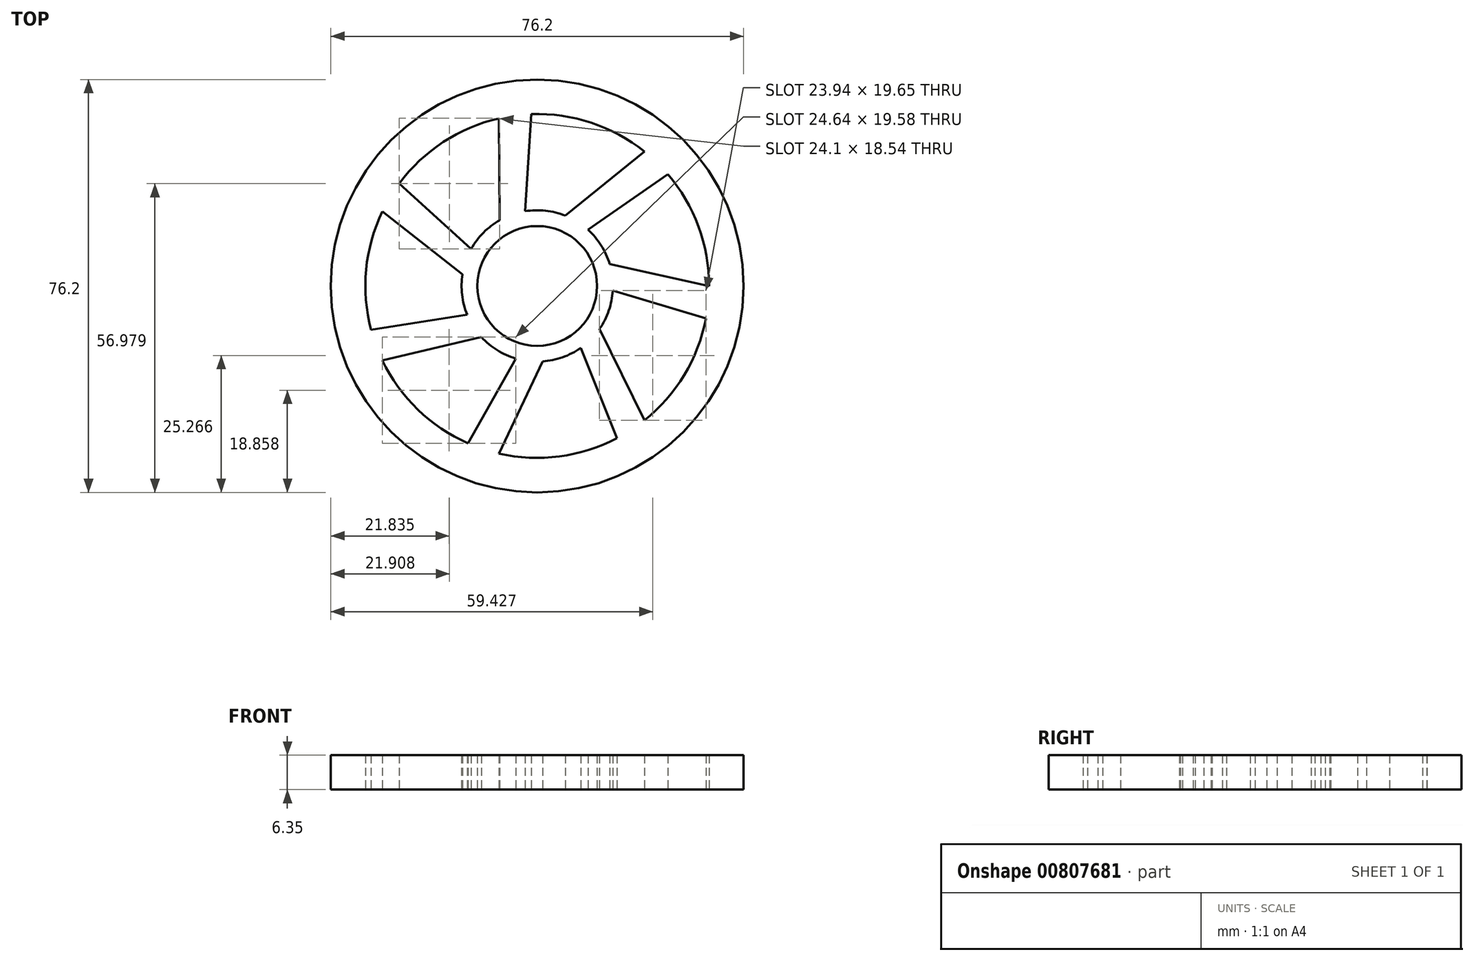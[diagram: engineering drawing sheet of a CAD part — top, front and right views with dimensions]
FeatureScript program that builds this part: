
annotation { "Feature Type Name" : "Feature", "Feature Type Description" : "" }
export const myFeature = defineFeature(function(context is Context, id is Id, definition is map)
    precondition{}
    {
        {
            var Q0;
            Q0=qCreatedBy(makeId("Top.planeOp"),FACE);
            var sketch = newSketch(context, id + "F0", { "sketchPlane" : qUnion([Q0])});
            skCircle(sketch, "E0", {"center": v(0, 0) * mm, "radius": 11.05 * mm});
            skCircle(sketch, "E1", {"center": v(0, 0) * mm, "radius": 31.73 * mm});
            skCircle(sketch, "E2", {"center": v(0, 0) * mm, "radius": 38.1 * mm});
            skLineSegment(sketch, "E3", {"start": v(0, 0) * mm, "end": v(-31.73, 0) * mm, "construction": true});
            skLineSegment(sketch, "E4", {"start": v(0, 0) * mm, "end": v(31.73, 0) * mm, "construction": true});
            skLineSegment(sketch, "E5", {"start": v(0, 0) * mm, "end": v(0, -31.73) * mm, "construction": true});
            skLineSegment(sketch, "E6.1.0", {"start": v(0, 0) * mm, "end": v(-31.75, 0) * mm, "construction": true});
            skLineSegment(sketch, "E6.2.0", {"start": v(0, 0) * mm, "end": v(0, -31.75) * mm, "construction": true});
            skLineSegment(sketch, "E6.3.0", {"start": v(0, 0) * mm, "end": v(31.75, 0) * mm, "construction": true});
            skLineSegment(sketch, "E7", {"start": v(0, 0) * mm, "end": v(0, 31.73) * mm, "construction": true});
            skLineSegment(sketch, "E8", {"start": v(9.95, 4.8) * mm, "end": v(31.73, 0) * mm});
            skLineSegment(sketch, "E9.1.0", {"start": v(2.45, 10.77) * mm, "end": v(19.78, 24.8) * mm});
            skLineSegment(sketch, "E9.2.0", {"start": v(-6.9, 8.63) * mm, "end": v(-7.06, 30.93) * mm});
            skLineSegment(sketch, "E9.3.0", {"start": v(-11.05, -0.01) * mm, "end": v(-28.58, 13.76) * mm});
            skLineSegment(sketch, "E9.4.0", {"start": v(-6.88, -8.65) * mm, "end": v(-28.58, -13.76) * mm});
            skLineSegment(sketch, "E9.5.0", {"start": v(2.47, -10.77) * mm, "end": v(-7.06, -30.93) * mm});
            skLineSegment(sketch, "E9.6.0", {"start": v(9.96, -4.78) * mm, "end": v(19.78, -24.8) * mm});
            skLineSegment(sketch, "E10", {"start": v(11.05, 0) * mm, "end": v(31.15, -6) * mm});
            skLineSegment(sketch, "E11.1.0", {"start": v(6.89, 8.64) * mm, "end": v(24.12, 20.61) * mm});
            skLineSegment(sketch, "E11.2.0", {"start": v(-2.46, 10.77) * mm, "end": v(-1.08, 31.7) * mm});
            skLineSegment(sketch, "E11.3.0", {"start": v(-9.95, 4.8) * mm, "end": v(-25.46, 18.93) * mm});
            skLineSegment(sketch, "E11.4.0", {"start": v(-9.95, -4.8) * mm, "end": v(-30.67, -8.1) * mm});
            skLineSegment(sketch, "E11.5.0", {"start": v(-2.46, -10.77) * mm, "end": v(-12.79, -29.03) * mm});
            skLineSegment(sketch, "E11.6.0", {"start": v(6.89, -8.64) * mm, "end": v(14.73, -28.1) * mm});
            skCircle(sketch, "E12", {"center": v(0, 0) * mm, "radius": 13.97 * mm});
            skSolve(sketch);
        }
        {
            var Q0;
            Q0=makeQuery(id+"F0.imprint","IMPRINT",FACE,{"disambiguationData":[TD([[makeQuery(id+"F0.imprint","IMPRINT",EDGE,{"derivedFrom":sQuery(id+"F0.wireOp",EDGE,"E2")}),1.0]])]});
            var Q1;
            {var subQ0=sQuery(id+"F0.wireOp",EDGE,"E9.4.0");Q1=makeQuery(id+"F0.imprint","IMPRINT",FACE,{"disambiguationData":[TD([[makeQuery(id+"F0.imprint","IMPRINT",EDGE,{"derivedFrom":subQ0}),-1.0]])]});}
            var Q2;
            {var subQ0=sQuery(id+"F0.wireOp",EDGE,"E9.3.0");Q2=makeQuery(id+"F0.imprint","IMPRINT",FACE,{"disambiguationData":[TD([[makeQuery(id+"F0.imprint","IMPRINT",EDGE,{"derivedFrom":subQ0}),-1.0]])]});}
            var Q3;
            {var subQ0=sQuery(id+"F0.wireOp",EDGE,"E9.2.0");Q3=makeQuery(id+"F0.imprint","IMPRINT",FACE,{"disambiguationData":[TD([[makeQuery(id+"F0.imprint","IMPRINT",EDGE,{"derivedFrom":subQ0}),-1.0]])]});}
            var Q4;
            {var subQ0=sQuery(id+"F0.wireOp",EDGE,"E9.1.0");Q4=makeQuery(id+"F0.imprint","IMPRINT",FACE,{"disambiguationData":[TD([[makeQuery(id+"F0.imprint","IMPRINT",EDGE,{"derivedFrom":subQ0}),-1.0]])]});}
            var Q5;
            {var subQ0=sQuery(id+"F0.wireOp",EDGE,"E8");Q5=makeQuery(id+"F0.imprint","IMPRINT",FACE,{"disambiguationData":[TD([[makeQuery(id+"F0.imprint","IMPRINT",EDGE,{"derivedFrom":subQ0}),-1.0]])]});}
            var Q6;
            {var subQ0=sQuery(id+"F0.wireOp",EDGE,"E9.6.0");Q6=makeQuery(id+"F0.imprint","IMPRINT",FACE,{"disambiguationData":[TD([[makeQuery(id+"F0.imprint","IMPRINT",EDGE,{"derivedFrom":subQ0}),-1.0]])]});}
            var Q7;
            {var subQ0=sQuery(id+"F0.wireOp",EDGE,"E9.5.0");Q7=makeQuery(id+"F0.imprint","IMPRINT",FACE,{"disambiguationData":[TD([[makeQuery(id+"F0.imprint","IMPRINT",EDGE,{"derivedFrom":subQ0}),-1.0]])]});}
            var Q8;
            {var subQ0=sQuery(id+"F0.wireOp",EDGE,"E9.2.0");var subQ1=sQuery(id+"F0.wireOp",EDGE,"E0");var subQ2=makeQuery(id+"F0.imprint","INTERSECT",VERTEX,{"derivedFrom":[subQ1,subQ0]});Q8=makeQuery(id+"F0.imprint","IMPRINT",FACE,{"disambiguationData":[TD([[makeQuery(id+"F0.imprint","IMPRINT",EDGE,{"disambiguationData":[TD([[subQ2,-1.0]])],"derivedFrom":subQ1}),-1.0]])]});}
            var Q9;
            {var subQ0=sQuery(id+"F0.wireOp",EDGE,"E9.3.0");var subQ1=sQuery(id+"F0.wireOp",EDGE,"E0");var subQ2=makeQuery(id+"F0.imprint","INTERSECT",VERTEX,{"derivedFrom":[subQ1,subQ0]});Q9=makeQuery(id+"F0.imprint","IMPRINT",FACE,{"disambiguationData":[TD([[makeQuery(id+"F0.imprint","IMPRINT",EDGE,{"disambiguationData":[TD([[subQ2,-1.0]])],"derivedFrom":subQ1}),-1.0]])]});}
            var Q10;
            {var subQ0=sQuery(id+"F0.wireOp",EDGE,"E9.4.0");var subQ1=sQuery(id+"F0.wireOp",EDGE,"E0");var subQ2=makeQuery(id+"F0.imprint","INTERSECT",VERTEX,{"derivedFrom":[subQ1,subQ0]});Q10=makeQuery(id+"F0.imprint","IMPRINT",FACE,{"disambiguationData":[TD([[makeQuery(id+"F0.imprint","IMPRINT",EDGE,{"disambiguationData":[TD([[subQ2,-1.0]])],"derivedFrom":subQ1}),-1.0]])]});}
            var Q11;
            {var subQ0=sQuery(id+"F0.wireOp",EDGE,"E9.5.0");var subQ1=sQuery(id+"F0.wireOp",EDGE,"E0");var subQ2=makeQuery(id+"F0.imprint","INTERSECT",VERTEX,{"derivedFrom":[subQ1,subQ0]});Q11=makeQuery(id+"F0.imprint","IMPRINT",FACE,{"disambiguationData":[TD([[makeQuery(id+"F0.imprint","IMPRINT",EDGE,{"disambiguationData":[TD([[subQ2,-1.0]])],"derivedFrom":subQ1}),-1.0]])]});}
            var Q12;
            {var subQ0=sQuery(id+"F0.wireOp",EDGE,"E9.6.0");var subQ1=sQuery(id+"F0.wireOp",EDGE,"E0");var subQ2=makeQuery(id+"F0.imprint","INTERSECT",VERTEX,{"derivedFrom":[subQ1,subQ0]});Q12=makeQuery(id+"F0.imprint","IMPRINT",FACE,{"disambiguationData":[TD([[makeQuery(id+"F0.imprint","IMPRINT",EDGE,{"disambiguationData":[TD([[subQ2,-1.0]])],"derivedFrom":subQ1}),-1.0]])]});}
            var Q13;
            {var subQ0=sQuery(id+"F0.wireOp",EDGE,"E8");var subQ1=sQuery(id+"F0.wireOp",EDGE,"E0");var subQ2=makeQuery(id+"F0.imprint","INTERSECT",VERTEX,{"derivedFrom":[subQ1,subQ0]});Q13=makeQuery(id+"F0.imprint","IMPRINT",FACE,{"disambiguationData":[TD([[makeQuery(id+"F0.imprint","IMPRINT",EDGE,{"disambiguationData":[TD([[subQ2,-1.0]])],"derivedFrom":subQ1}),-1.0]])]});}
            var Q14;
            {var subQ0=sQuery(id+"F0.wireOp",EDGE,"E9.1.0");var subQ1=sQuery(id+"F0.wireOp",EDGE,"E0");var subQ2=makeQuery(id+"F0.imprint","INTERSECT",VERTEX,{"derivedFrom":[subQ1,subQ0]});Q14=makeQuery(id+"F0.imprint","IMPRINT",FACE,{"disambiguationData":[TD([[makeQuery(id+"F0.imprint","IMPRINT",EDGE,{"disambiguationData":[TD([[subQ2,-1.0]])],"derivedFrom":subQ1}),-1.0]])]});}
            extrude(context, id + "F1", {"entities" : qUnion([Q0, Q1, Q2, Q3, Q4, Q5, Q6, Q7, Q8, Q9, Q10, Q11, Q12, Q13, Q14]), "depth" : 6.35 * mm, "offsetDistance" : 25.4 * mm});
        }
    });
